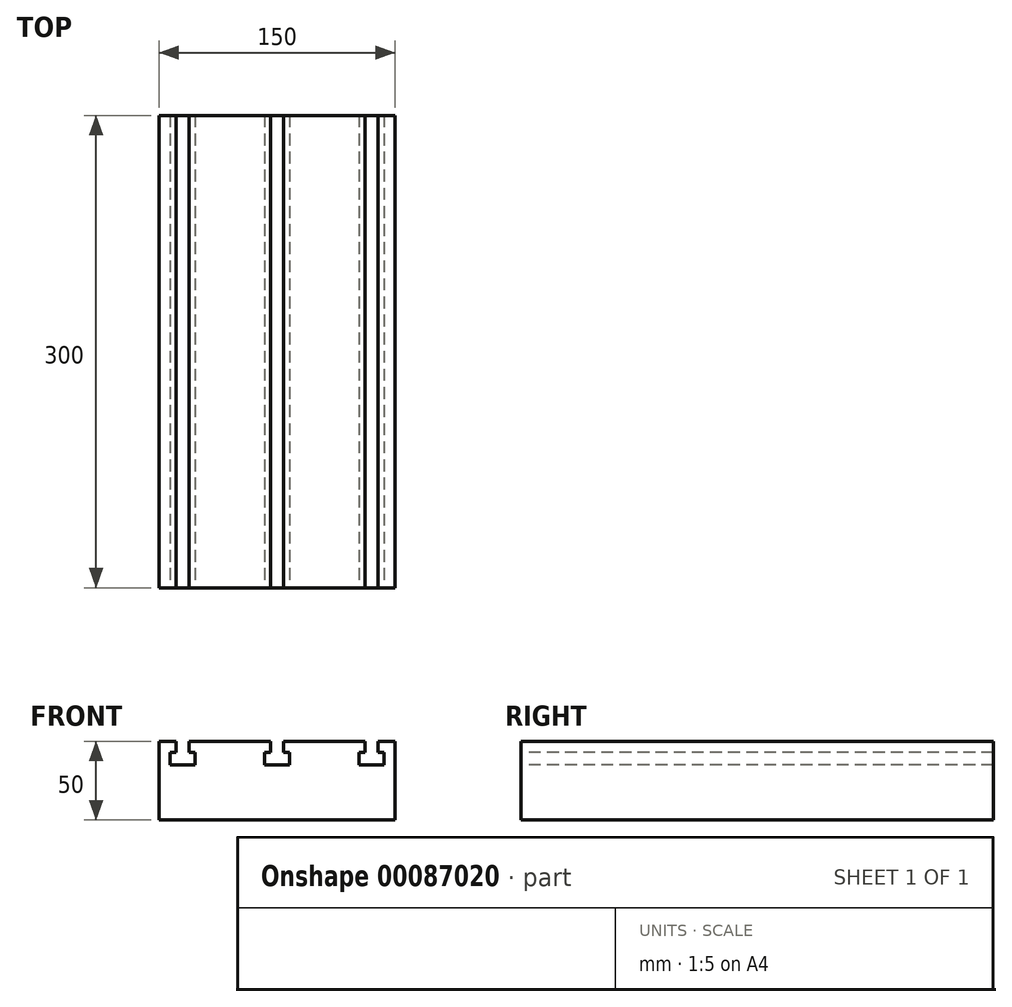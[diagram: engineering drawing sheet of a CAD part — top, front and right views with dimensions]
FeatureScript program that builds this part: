
annotation { "Feature Type Name" : "Feature", "Feature Type Description" : "" }
export const myFeature = defineFeature(function(context is Context, id is Id, definition is map)
    precondition{}
    {
        {
            var Q0;
            Q0=qCreatedBy(makeId("Front.planeOp"),FACE);
            var sketch = newSketch(context, id + "F0", { "sketchPlane" : qUnion([Q0])});
            skLineSegment(sketch, "E0.bottom", {"start": v(-75, -25) * mm, "end": v(75, -25) * mm});
            skLineSegment(sketch, "E0.top", {"start": v(-75, 25) * mm, "end": v(-64.2, 25) * mm});
            skLineSegment(sketch, "E0.left", {"start": v(-75, -25) * mm, "end": v(-75, 25) * mm});
            skLineSegment(sketch, "E0.right", {"start": v(75, -25) * mm, "end": v(75, 25) * mm});
            skPoint(sketch, "E0.middle", {"position": v(0, 0) * mm});
            skLineSegment(sketch, "E1.bottom", {"start": v(-8, 10) * mm, "end": v(8, 10) * mm});
            skLineSegment(sketch, "E1.top", {"start": v(-8, 18) * mm, "end": v(-4.2, 18) * mm});
            skLineSegment(sketch, "E1.left", {"start": v(-8, 10) * mm, "end": v(-8, 18) * mm});
            skLineSegment(sketch, "E1.right", {"start": v(8, 10) * mm, "end": v(8, 18) * mm});
            skPoint(sketch, "E1.middle", {"position": v(0, 14) * mm});
            skLineSegment(sketch, "E2", {"start": v(-4.2, 18) * mm, "end": v(-4.2, 25) * mm});
            skLineSegment(sketch, "E3.MirrorCS", {"start": v(4.2, 18) * mm, "end": v(4.2, 25) * mm});
            skPoint(sketch, "E4.orphan", {"position": v(-4.2, 32.97) * mm});
            skPoint(sketch, "E5.orphan", {"position": v(4.2, 32.97) * mm});
            skLineSegment(sketch, "E6.trimOffspring", {"start": v(4.2, 25) * mm, "end": v(55.8, 25) * mm});
            skLineSegment(sketch, "E7.trimOffspring", {"start": v(4.2, 18) * mm, "end": v(8, 18) * mm});
            skLineSegment(sketch, "E8.1.0.0", {"start": v(55.8, 18) * mm, "end": v(55.8, 25) * mm});
            skLineSegment(sketch, "E8.1.0.1", {"start": v(64.2, 18) * mm, "end": v(64.2, 25) * mm});
            skLineSegment(sketch, "E8.1.0.2", {"start": v(52, 10) * mm, "end": v(68, 10) * mm});
            skLineSegment(sketch, "E8.1.0.3", {"start": v(68, 10) * mm, "end": v(68, 18) * mm});
            skLineSegment(sketch, "E8.1.0.4", {"start": v(52, 10) * mm, "end": v(52, 18) * mm});
            skPoint(sketch, "E8.1.0.5", {"position": v(60, 14) * mm});
            skLineSegment(sketch, "E8.1.0.6", {"start": v(52, 18) * mm, "end": v(55.8, 18) * mm});
            skLineSegment(sketch, "E8.1.0.7", {"start": v(64.2, 18) * mm, "end": v(68, 18) * mm});
            skLineSegment(sketch, "E8.direction1", {"start": v(-4.2, 18) * mm, "end": v(55.8, 18) * mm, "construction": true});
            skLineSegment(sketch, "E9.trimOffspring", {"start": v(64.2, 25) * mm, "end": v(75, 25) * mm});
            skLineSegment(sketch, "E10.MirrorCS", {"start": v(-68, 10) * mm, "end": v(-68, 18) * mm});
            skPoint(sketch, "E11.MirrorP", {"position": v(-60, 14) * mm});
            skLineSegment(sketch, "E12.MirrorCS", {"start": v(-52, 10) * mm, "end": v(-68, 10) * mm});
            skLineSegment(sketch, "E13.MirrorCS", {"start": v(-52, 18) * mm, "end": v(-55.8, 18) * mm});
            skLineSegment(sketch, "E14.MirrorCS", {"start": v(-64.2, 18) * mm, "end": v(-68, 18) * mm});
            skLineSegment(sketch, "E15.MirrorCS", {"start": v(-52, 10) * mm, "end": v(-52, 18) * mm});
            skLineSegment(sketch, "E16.MirrorCS", {"start": v(-55.8, 18) * mm, "end": v(-55.8, 25) * mm});
            skLineSegment(sketch, "E17.MirrorCS", {"start": v(-64.2, 18) * mm, "end": v(-64.2, 25) * mm});
            skLineSegment(sketch, "E18.trimOffspring", {"start": v(-55.8, 25) * mm, "end": v(-4.2, 25) * mm});
            skLineSegment(sketch, "E19", {"start": v(35.96, -25) * mm, "end": v(46.09, -39.94) * mm});
            skLineSegment(sketch, "E20", {"start": v(46.09, -39.94) * mm, "end": v(10.9, -39.94) * mm});
            skLineSegment(sketch, "E21", {"start": v(10.9, -39.94) * mm, "end": v(10.9, -25) * mm});
            skSolve(sketch);
        }
        {
            var Q0;
            Q0=makeQuery(id+"F0.imprint","IMPRINT",FACE,{"disambiguationData":[TD([[makeQuery(id+"F0.imprint","IMPRINT",EDGE,{"derivedFrom":sQuery(id+"F0.wireOp",EDGE,"E0.bottom")}),1.0]])]});
            extrude(context, id + "F1", {"entities" : qUnion([Q0]), "oppositeDirection" : true, "depth" : 150 * mm, "hasSecondDirection" : true, "secondDirectionOppositeDirection" : false, "secondDirectionDepth" : 150 * mm});
        }
    });
